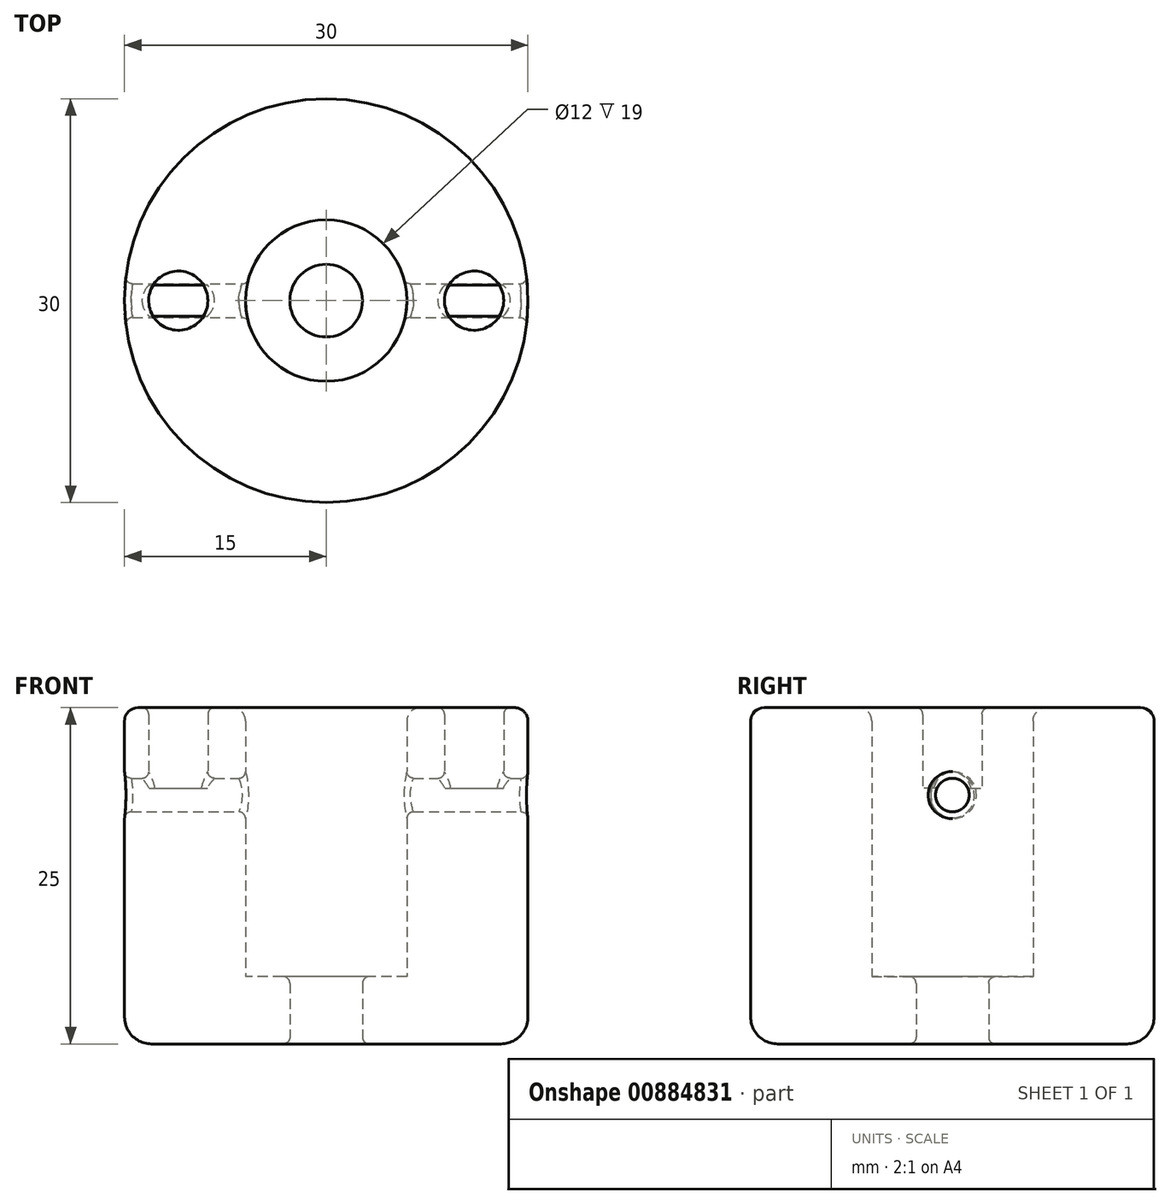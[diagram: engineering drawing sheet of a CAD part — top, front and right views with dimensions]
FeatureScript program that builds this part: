
annotation { "Feature Type Name" : "Feature", "Feature Type Description" : "" }
export const myFeature = defineFeature(function(context is Context, id is Id, definition is map)
    precondition{}
    {
        {
            var Q0;
            Q0=qCreatedBy(makeId("Top.planeOp"),FACE);
            var sketch = newSketch(context, id + "F0", { "sketchPlane" : qUnion([Q0])});
            skCircle(sketch, "E0", {"center": v(0, 0) * mm, "radius": 2.7 * mm});
            skCircle(sketch, "E1", {"center": v(0, 0) * mm, "radius": 15 * mm});
            skCircle(sketch, "E2", {"center": v(0, 0) * mm, "radius": 6 * mm});
            skSolve(sketch);
        }
        {
            var Q0;
            Q0=makeQuery(id+"F0.imprint","IMPRINT",FACE,{"disambiguationData":[TD([[makeQuery(id+"F0.imprint","IMPRINT",EDGE,{"derivedFrom":sQuery(id+"F0.wireOp",EDGE,"E0")}),-1.0]])]});
            extrude(context, id + "F1", {"entities" : qUnion([Q0]), "depth" : 5 * mm, "offsetDistance" : 25 * mm});
        }
        {
            var Q0;
            Q0 = qSketchRegion(id + "F0", true);
            extrude(context, id + "F2", {"entities" : qUnion([Q0]), "operationType" : NewBodyOperationType.ADD, "depth" : 25 * mm, "offsetDistance" : 25 * mm});
        }
        {
            var Q0;
            Q0=qCreatedBy(makeId("Right.planeOp"),FACE);
            var sketch = newSketch(context, id + "F3", { "sketchPlane" : qUnion([Q0])});
            skCircle(sketch, "E3", {"center": v(0, 18.5) * mm, "radius": 1.25 * mm});
            skLineSegment(sketch, "E4", {"start": v(0, 18.5) * mm, "end": v(0, 0) * mm});
            skSolve(sketch);
        }
        {
            var Q0;
            Q0 = qSketchRegion(id + "F3", true);
            extrude(context, id + "F4", {"entities" : qUnion([Q0]), "operationType" : NewBodyOperationType.REMOVE, "endBound" : BoundingType.SYMMETRIC, "oppositeDirection" : true, "depth" : 40 * mm, "offsetDistance" : 25 * mm});
        }
        {
            var Q0;
            Q0=qCreatedBy(makeId("Top.planeOp"),FACE);
            var sketch = newSketch(context, id + "F5", { "sketchPlane" : qUnion([Q0])});
            skCircle(sketch, "E5", {"center": v(11, 0) * mm, "radius": 2.2 * mm});
            skCircle(sketch, "E6.MirrorC", {"center": v(-11, 0) * mm, "radius": 2.2 * mm});
            skSolve(sketch);
        }
        {
            var Q0;
            Q0 = qSketchRegion(id + "F5", true);
            extrude(context, id + "F6", {"entities" : qUnion([Q0]), "operationType" : NewBodyOperationType.REMOVE, "endBound" : BoundingType.THROUGH_ALL, "depth" : 25 * mm, "offsetDistance" : 25 * mm, "hasSecondDirection" : true, "secondDirectionOppositeDirection" : false, "secondDirectionDepth" : 19 * mm});
        }
        {
            var Q0;
            Q0=makeQuery(id+"F2.opExtrude","CAP_EDGE",EDGE,{"disambiguationData":[OSD([sQuery(id+"F0.wireOp",EDGE,"E1")])],"isStart":false});
            var Q1;
            Q1=makeQuery(id+"F2.opExtrude","CAP_EDGE",EDGE,{"disambiguationData":[OSD([sQuery(id+"F0.wireOp",EDGE,"E2")])],"isStart":false});
            fillet(context, id + "F7", {"entities" : qUnion([Q0, Q1]), "radius" : 1 * mm, "tangentPropagation" : true, "allowEdgeOverflow" : false});
        }
        {
            var Q0;
            Q0=makeQuery(id+"F6.boolean.opBoolean","INTERSECT",EDGE,{"derivedFrom":[makeQuery(id+"F2.opExtrude","CAP_FACE",FACE,{"disambiguationData":[OSD([sQuery(id+"F0.wireOp",EDGE,"E1"),sQuery(id+"F0.wireOp",EDGE,"E2")])],"isStart":false}),makeQuery(id+"F6.opExtrude","SWEPT_FACE",FACE,{"disambiguationData":[OSD([sQuery(id+"F5.wireOp",EDGE,"E5")])]})]});
            var Q1;
            Q1=makeQuery(id+"F6.boolean.opBoolean","INTERSECT",EDGE,{"derivedFrom":[makeQuery(id+"F2.opExtrude","CAP_FACE",FACE,{"disambiguationData":[OSD([sQuery(id+"F0.wireOp",EDGE,"E1"),sQuery(id+"F0.wireOp",EDGE,"E2")])],"isStart":false}),makeQuery(id+"F6.opExtrude","SWEPT_FACE",FACE,{"disambiguationData":[OSD([sQuery(id+"F5.wireOp",EDGE,"E6.MirrorC")])]})]});
            var Q2;
            Q2=makeQuery(id+"F4.boolean.opBoolean","INTERSECT",EDGE,{"disambiguationData":[OD(0.0)],"derivedFrom":[makeQuery(id+"F2.opExtrude","SWEPT_FACE",FACE,{"disambiguationData":[OSD([sQuery(id+"F0.wireOp",EDGE,"E2")])]}),makeQuery(id+"F4.opExtrude","SWEPT_FACE",FACE,{"disambiguationData":[OSD([sQuery(id+"F3.wireOp",EDGE,"E3")])]})]});
            var Q3;
            Q3=makeQuery(id+"F4.boolean.opBoolean","INTERSECT",EDGE,{"disambiguationData":[OD(1.0)],"derivedFrom":[makeQuery(id+"F2.opExtrude","SWEPT_FACE",FACE,{"disambiguationData":[OSD([sQuery(id+"F0.wireOp",EDGE,"E1")])]}),makeQuery(id+"F4.opExtrude","SWEPT_FACE",FACE,{"disambiguationData":[OSD([sQuery(id+"F3.wireOp",EDGE,"E3")])]})]});
            var Q4;
            Q4=makeQuery(id+"F4.boolean.opBoolean","INTERSECT",EDGE,{"disambiguationData":[OD(1.0)],"derivedFrom":[makeQuery(id+"F2.opExtrude","SWEPT_FACE",FACE,{"disambiguationData":[OSD([sQuery(id+"F0.wireOp",EDGE,"E2")])]}),makeQuery(id+"F4.opExtrude","SWEPT_FACE",FACE,{"disambiguationData":[OSD([sQuery(id+"F3.wireOp",EDGE,"E3")])]})]});
            var Q5;
            Q5=makeQuery(id+"F4.boolean.opBoolean","INTERSECT",EDGE,{"disambiguationData":[OD(0.0)],"derivedFrom":[makeQuery(id+"F2.opExtrude","SWEPT_FACE",FACE,{"disambiguationData":[OSD([sQuery(id+"F0.wireOp",EDGE,"E1")])]}),makeQuery(id+"F4.opExtrude","SWEPT_FACE",FACE,{"disambiguationData":[OSD([sQuery(id+"F3.wireOp",EDGE,"E3")])]})]});
            var Q6;
            Q6=makeQuery(id+"F1.opExtrude","CAP_EDGE",EDGE,{"disambiguationData":[OSD([sQuery(id+"F0.wireOp",EDGE,"E0")])],"isStart":true});
            var Q7;
            Q7=makeQuery(id+"F1.opExtrude","CAP_EDGE",EDGE,{"disambiguationData":[OSD([sQuery(id+"F0.wireOp",EDGE,"E0")])],"isStart":false});
            var Q8;
            Q8=makeQuery(id+"F6.boolean.opBoolean","INTERSECT",EDGE,{"disambiguationData":[OD(0.0)],"derivedFrom":[makeQuery(id+"F4.boolean.opBoolean","COPY",FACE,{"disambiguationData":[OD(1.0)],"derivedFrom":makeQuery(id+"F4.opExtrude","SWEPT_FACE",FACE,{"disambiguationData":[OSD([sQuery(id+"F3.wireOp",EDGE,"E3")])]})}),makeQuery(id+"F6.opExtrude","SWEPT_FACE",FACE,{"disambiguationData":[OSD([sQuery(id+"F5.wireOp",EDGE,"E5")])]})]});
            var Q9;
            Q9=makeQuery(id+"F6.boolean.opBoolean","INTERSECT",EDGE,{"disambiguationData":[OD(1.0)],"derivedFrom":[makeQuery(id+"F4.boolean.opBoolean","COPY",FACE,{"disambiguationData":[OD(0.0)],"derivedFrom":makeQuery(id+"F4.opExtrude","SWEPT_FACE",FACE,{"disambiguationData":[OSD([sQuery(id+"F3.wireOp",EDGE,"E3")])]})}),makeQuery(id+"F6.opExtrude","SWEPT_FACE",FACE,{"disambiguationData":[OSD([sQuery(id+"F5.wireOp",EDGE,"E6.MirrorC")])]})]});
            var Q10;
            Q10=makeQuery(id+"F6.boolean.opBoolean","INTERSECT",EDGE,{"disambiguationData":[OD(1.0)],"derivedFrom":[makeQuery(id+"F4.boolean.opBoolean","COPY",FACE,{"disambiguationData":[OD(1.0)],"derivedFrom":makeQuery(id+"F4.opExtrude","SWEPT_FACE",FACE,{"disambiguationData":[OSD([sQuery(id+"F3.wireOp",EDGE,"E3")])]})}),makeQuery(id+"F6.opExtrude","SWEPT_FACE",FACE,{"disambiguationData":[OSD([sQuery(id+"F5.wireOp",EDGE,"E5")])]})]});
            var Q11;
            Q11=makeQuery(id+"F6.boolean.opBoolean","INTERSECT",EDGE,{"disambiguationData":[OD(0.0)],"derivedFrom":[makeQuery(id+"F4.boolean.opBoolean","COPY",FACE,{"disambiguationData":[OD(0.0)],"derivedFrom":makeQuery(id+"F4.opExtrude","SWEPT_FACE",FACE,{"disambiguationData":[OSD([sQuery(id+"F3.wireOp",EDGE,"E3")])]})}),makeQuery(id+"F6.opExtrude","SWEPT_FACE",FACE,{"disambiguationData":[OSD([sQuery(id+"F5.wireOp",EDGE,"E6.MirrorC")])]})]});
            fillet(context, id + "F8", {"entities" : qUnion([Q0, Q1, Q2, Q3, Q4, Q5, Q6, Q7, Q8, Q9, Q10, Q11]), "radius" : 0.5 * mm, "tangentPropagation" : true, "allowEdgeOverflow" : false});
        }
        {
            var Q0;
            Q0=makeQuery(id+"F2.opExtrude","CAP_EDGE",EDGE,{"disambiguationData":[OSD([sQuery(id+"F0.wireOp",EDGE,"E1")])],"isStart":true});
            fillet(context, id + "F9", {"entities" : qUnion([Q0]), "radius" : 2 * mm, "tangentPropagation" : true, "allowEdgeOverflow" : false});
        }
    });
